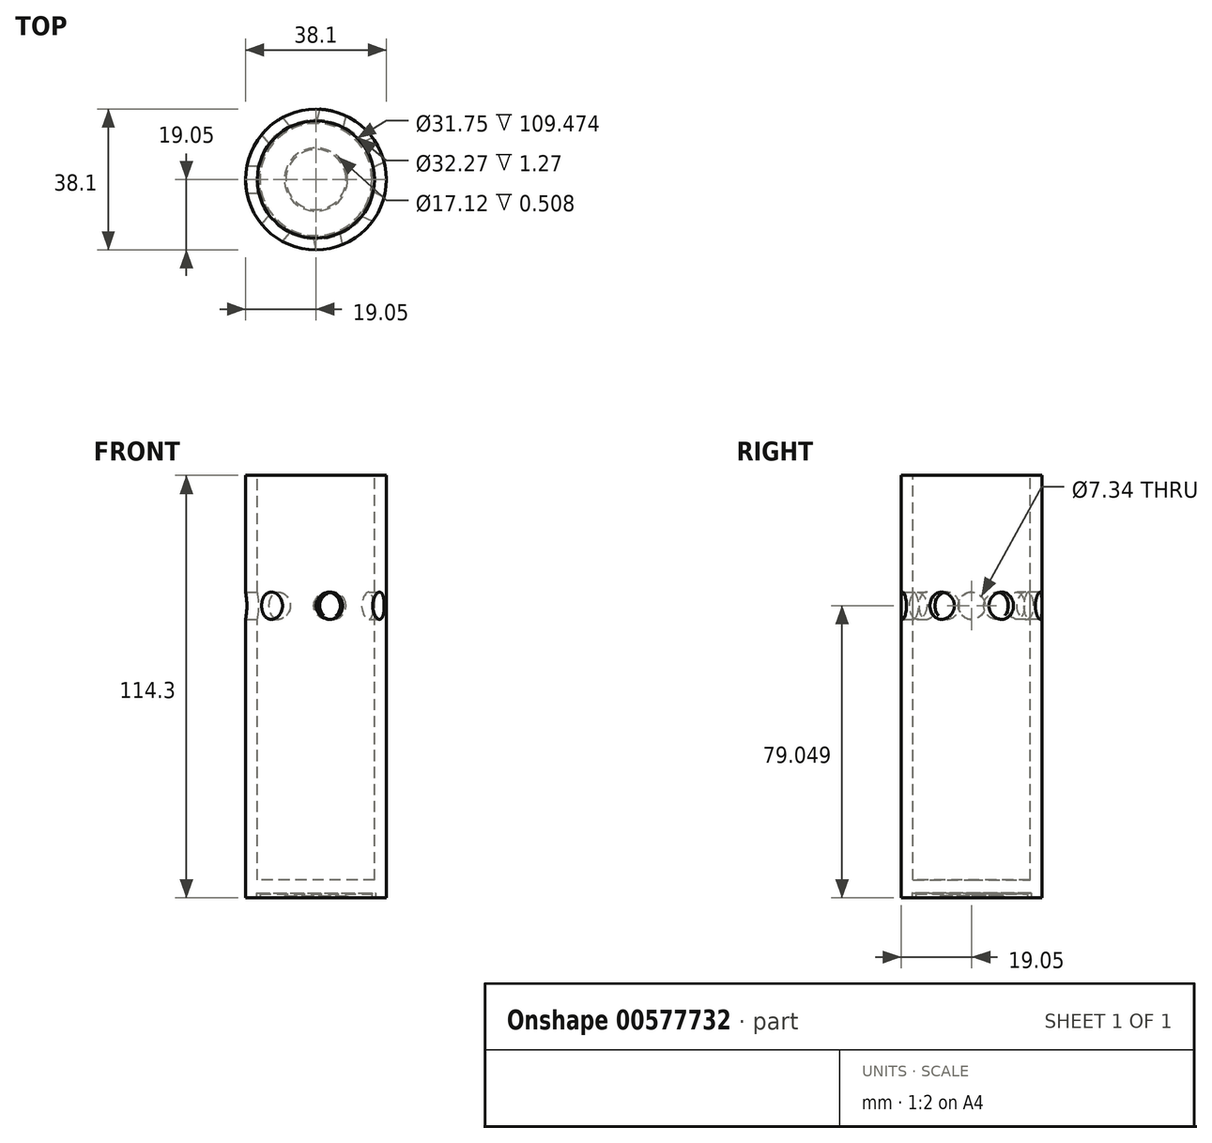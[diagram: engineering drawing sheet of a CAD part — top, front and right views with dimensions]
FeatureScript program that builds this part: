
annotation { "Feature Type Name" : "Feature", "Feature Type Description" : "" }
export const myFeature = defineFeature(function(context is Context, id is Id, definition is map)
    precondition{}
    {
        {
            var Q0;
            Q0=qCreatedBy(makeId("Top.planeOp"),FACE);
            var sketch = newSketch(context, id + "F0", { "sketchPlane" : qUnion([Q0])});
            skCircle(sketch, "E0", {"center": v(0, 0) * mm, "radius": 19.05 * mm});
            skSolve(sketch);
        }
        {
            var Q0;
            Q0=makeQuery(id+"F0.imprint","IMPRINT",FACE,{"disambiguationData":[TD([[makeQuery(id+"F0.imprint","IMPRINT",EDGE,{"derivedFrom":sQuery(id+"F0.wireOp",EDGE,"E0")}),1.0]])]});
            extrude(context, id + "F1", {"entities" : qUnion([Q0]), "depth" : 109.47 * mm, "offsetDistance" : 25.4 * mm});
        }
        {
            var Q0;
            Q0=makeQuery(id+"F1.opExtrude","CAP_FACE",FACE,{"disambiguationData":[OSD([sQuery(id+"F0.wireOp",EDGE,"E0")])],"isStart":false});
            var sketch = newSketch(context, id + "F2", { "sketchPlane" : qUnion([Q0])});
            skCircle(sketch, "E1", {"center": v(0, 0) * mm, "radius": 15.87 * mm});
            skSolve(sketch);
        }
        {
            var Q0;
            Q0=makeQuery(id+"F2.imprint","IMPRINT",FACE,{"disambiguationData":[TD([[makeQuery(id+"F2.imprint","IMPRINT",EDGE,{"derivedFrom":sQuery(id+"F2.wireOp",EDGE,"E1")}),1.0]])]});
            extrude(context, id + "F3", {"entities" : qUnion([Q0]), "operationType" : NewBodyOperationType.REMOVE, "oppositeDirection" : true, "depth" : 109.73 * mm, "offsetDistance" : 25.4 * mm});
        }
        {
            var Q0;
            Q0=qCreatedBy(makeId("Top.planeOp"),FACE);
            var sketch = newSketch(context, id + "F4", { "sketchPlane" : qUnion([Q0])});
            skCircle(sketch, "E2", {"center": v(0, 0) * mm, "radius": 19.05 * mm});
            skSolve(sketch);
        }
        {
            var Q0;
            Q0=makeQuery(id+"F4.imprint","IMPRINT",FACE,{"disambiguationData":[TD([[makeQuery(id+"F4.imprint","IMPRINT",EDGE,{"derivedFrom":sQuery(id+"F4.wireOp",EDGE,"E2")}),1.0]])]});
            extrude(context, id + "F5", {"entities" : qUnion([Q0]), "operationType" : NewBodyOperationType.ADD, "oppositeDirection" : true, "depth" : 1.27 * mm, "offsetDistance" : 25.4 * mm});
        }
        {
            var Q0;
            Q0=qCreatedBy(makeId("Right.planeOp"),FACE);
            var Q1;
            Q1=qCreatedBy(makeId("Front.planeOp"),FACE);
            cPlane(context, id + "F6", {"entities" : qUnion([Q0, Q1]), "cplaneType" : CPlaneType.MID_PLANE, "offset" : 25.4 * mm, "flipAlignment" : true, "width" : 152.4 * mm, "height" : 152.4 * mm});
        }
        {
            var Q0;
            Q0=qCreatedBy(makeId("Right.planeOp"),FACE);
            var Q1;
            Q1=qCreatedBy(makeId("Front.planeOp"),FACE);
            cPlane(context, id + "F7", {"entities" : qUnion([Q0, Q1]), "cplaneType" : CPlaneType.MID_PLANE, "offset" : 25.4 * mm, "width" : 152.4 * mm, "height" : 152.4 * mm});
        }
        {
            var Q0;
            Q0=qCreatedBy(id+"F7.planeOp",FACE);
            var Q1;
            Q1=qCreatedBy(makeId("Right.planeOp"),FACE);
            cPlane(context, id + "F8", {"entities" : qUnion([Q0, Q1]), "cplaneType" : CPlaneType.MID_PLANE, "offset" : 25.4 * mm, "flipAlignment" : true, "width" : 152.4 * mm, "height" : 152.4 * mm});
        }
        {
            var Q0;
            Q0=qCreatedBy(id+"F6.planeOp",FACE);
            var Q1;
            Q1=qCreatedBy(makeId("Right.planeOp"),FACE);
            cPlane(context, id + "F9", {"entities" : qUnion([Q0, Q1]), "cplaneType" : CPlaneType.MID_PLANE, "offset" : 25.4 * mm, "flipAlignment" : true, "width" : 152.4 * mm, "height" : 152.4 * mm});
        }
        {
            var Q0;
            Q0=qCreatedBy(makeId("Front.planeOp"),FACE);
            var Q1;
            Q1=qCreatedBy(id+"F7.planeOp",FACE);
            cPlane(context, id + "F10", {"entities" : qUnion([Q0, Q1]), "cplaneType" : CPlaneType.MID_PLANE, "offset" : 25.4 * mm, "width" : 152.4 * mm, "height" : 152.4 * mm});
        }
        {
            var Q0;
            Q0=qCreatedBy(makeId("Front.planeOp"),FACE);
            var Q1;
            Q1=qCreatedBy(id+"F6.planeOp",FACE);
            cPlane(context, id + "F11", {"entities" : qUnion([Q0, Q1]), "cplaneType" : CPlaneType.MID_PLANE, "offset" : 25.4 * mm, "flipAlignment" : true, "width" : 152.4 * mm, "height" : 152.4 * mm});
        }
        {
            var Q0;
            Q0=qCreatedBy(id+"F8.planeOp",FACE);
            var Q1;
            Q1=qCreatedBy(id+"F7.planeOp",FACE);
            cPlane(context, id + "F12", {"entities" : qUnion([Q0, Q1]), "cplaneType" : CPlaneType.MID_PLANE, "offset" : 25.4 * mm, "flipAlignment" : true, "width" : 152.4 * mm, "height" : 152.4 * mm});
        }
        {
            var Q0;
            Q0=qCreatedBy(id+"F9.planeOp",FACE);
            var Q1;
            Q1=qCreatedBy(id+"F6.planeOp",FACE);
            cPlane(context, id + "F13", {"entities" : qUnion([Q0, Q1]), "cplaneType" : CPlaneType.MID_PLANE, "offset" : 25.4 * mm, "flipAlignment" : true, "width" : 152.4 * mm, "height" : 152.4 * mm});
        }
        {
            var Q0;
            Q0=qCreatedBy(id+"F13.planeOp",FACE);
            var Q1;
            Q1=qCreatedBy(id+"F9.planeOp",FACE);
            cPlane(context, id + "F14", {"entities" : qUnion([Q0, Q1]), "cplaneType" : CPlaneType.MID_PLANE, "offset" : 25.4 * mm, "flipAlignment" : true, "width" : 152.4 * mm, "height" : 152.4 * mm});
        }
        {
            var Q0;
            Q0=qCreatedBy(id+"F8.planeOp",FACE);
            var Q1;
            Q1=qCreatedBy(id+"F12.planeOp",FACE);
            cPlane(context, id + "F15", {"entities" : qUnion([Q0, Q1]), "cplaneType" : CPlaneType.MID_PLANE, "offset" : 25.4 * mm, "flipAlignment" : true, "width" : 152.4 * mm, "height" : 152.4 * mm});
        }
        {
            var Q0;
            Q0=qCreatedBy(id+"F15.planeOp",FACE);
            var Q1;
            Q1=qCreatedBy(id+"F8.planeOp",FACE);
            cPlane(context, id + "F16", {"entities" : qUnion([Q0, Q1]), "cplaneType" : CPlaneType.MID_PLANE, "offset" : 25.4 * mm, "flipAlignment" : true, "width" : 152.4 * mm, "height" : 152.4 * mm});
        }
        {
            var Q0;
            Q0=qCreatedBy(id+"F9.planeOp",FACE);
            var Q1;
            Q1=qCreatedBy(id+"F14.planeOp",FACE);
            cPlane(context, id + "F17", {"entities" : qUnion([Q0, Q1]), "cplaneType" : CPlaneType.MID_PLANE, "offset" : 25.4 * mm, "flipAlignment" : true, "width" : 152.4 * mm, "height" : 152.4 * mm});
        }
        {
            var Q0;
            Q0=qCreatedBy(makeId("Front.planeOp"),FACE);
            var Q1;
            Q1=qCreatedBy(id+"F11.planeOp",FACE);
            cPlane(context, id + "F18", {"entities" : qUnion([Q0, Q1]), "cplaneType" : CPlaneType.MID_PLANE, "offset" : 25.4 * mm, "flipAlignment" : true, "width" : 152.4 * mm, "height" : 152.4 * mm});
        }
        {
            var Q0;
            Q0=qCreatedBy(id+"F10.planeOp",FACE);
            var Q1;
            Q1=qCreatedBy(id+"F7.planeOp",FACE);
            cPlane(context, id + "F19", {"entities" : qUnion([Q0, Q1]), "cplaneType" : CPlaneType.MID_PLANE, "offset" : 25.4 * mm, "width" : 152.4 * mm, "height" : 152.4 * mm});
        }
        {
            var Q0;
            Q0=qCreatedBy(id+"F19.planeOp",FACE);
            var Q1;
            Q1=qCreatedBy(id+"F7.planeOp",FACE);
            cPlane(context, id + "F20", {"entities" : qUnion([Q0, Q1]), "cplaneType" : CPlaneType.MID_PLANE, "offset" : 25.4 * mm, "width" : 152.4 * mm, "height" : 152.4 * mm});
        }
        {
            var Q0;
            Q0=qCreatedBy(id+"F6.planeOp",FACE);
            var Q1;
            Q1=qCreatedBy(id+"F11.planeOp",FACE);
            cPlane(context, id + "F21", {"entities" : qUnion([Q0, Q1]), "cplaneType" : CPlaneType.MID_PLANE, "offset" : 25.4 * mm, "flipAlignment" : true, "width" : 152.4 * mm, "height" : 152.4 * mm});
        }
        {
            var Q0;
            Q0=qCreatedBy(id+"F6.planeOp",FACE);
            var Q1;
            Q1=qCreatedBy(id+"F21.planeOp",FACE);
            cPlane(context, id + "F22", {"entities" : qUnion([Q0, Q1]), "cplaneType" : CPlaneType.MID_PLANE, "offset" : 25.4 * mm, "flipAlignment" : true, "width" : 152.4 * mm, "height" : 152.4 * mm});
        }
        {
            var Q0;
            Q0=qCreatedBy(id+"F20.planeOp",FACE);
            var Q1;
            Q1=qCreatedBy(id+"F18.planeOp",FACE);
            cPlane(context, id + "F23", {"entities" : qUnion([Q0, Q1]), "cplaneType" : CPlaneType.MID_PLANE, "offset" : 25.4 * mm, "flipAlignment" : true, "width" : 152.4 * mm, "height" : 152.4 * mm});
        }
        {
            var Q0;
            Q0=qCreatedBy(id+"F17.planeOp",FACE);
            var sketch = newSketch(context, id + "F24", { "sketchPlane" : qUnion([Q0])});
            skCircle(sketch, "E3", {"center": v(0, 74.22) * mm, "radius": 3.67 * mm});
            skLineSegment(sketch, "E4", {"start": v(0, 74.22) * mm, "end": v(0, 0) * mm});
            skSolve(sketch);
        }
        {
            var Q0;
            Q0 = qSketchRegion(id + "F24", true);
            extrude(context, id + "F25", {"entities" : qUnion([Q0]), "operationType" : NewBodyOperationType.ADD, "depth" : 25.4 * mm, "offsetDistance" : 25.4 * mm});
        }
        {
            var Q0;
            Q0=makeQuery(id+"F25.opExtrude","CAP_FACE",FACE,{"disambiguationData":[OSD([sQuery(id+"F24.wireOp",EDGE,"E3")])],"isStart":false});
            extrude(context, id + "F26", {"entities" : qUnion([Q0]), "operationType" : NewBodyOperationType.REMOVE, "oppositeDirection" : true, "depth" : 32 * mm, "offsetDistance" : 25.4 * mm});
        }
        {
            var Q0;
            Q0=qCreatedBy(id+"F16.planeOp",FACE);
            var sketch = newSketch(context, id + "F27", { "sketchPlane" : qUnion([Q0])});
            skCircle(sketch, "E5", {"center": v(0, 74.22) * mm, "radius": 3.67 * mm});
            skLineSegment(sketch, "E6", {"start": v(0, 74.22) * mm, "end": v(0, 0) * mm});
            skSolve(sketch);
        }
        {
            var Q0;
            Q0 = qSketchRegion(id + "F27", true);
            extrude(context, id + "F28", {"entities" : qUnion([Q0]), "operationType" : NewBodyOperationType.REMOVE, "depth" : 45.47 * mm, "offsetDistance" : 25.4 * mm});
        }
        {
            var Q0;
            Q0=qCreatedBy(id+"F23.planeOp",FACE);
            var sketch = newSketch(context, id + "F29", { "sketchPlane" : qUnion([Q0])});
            skCircle(sketch, "E7", {"center": v(0, 74.22) * mm, "radius": 3.67 * mm});
            skLineSegment(sketch, "E8", {"start": v(0, 74.22) * mm, "end": v(0, 0) * mm});
            skSolve(sketch);
        }
        {
            var Q0;
            Q0 = qSketchRegion(id + "F29", true);
            extrude(context, id + "F30", {"entities" : qUnion([Q0]), "operationType" : NewBodyOperationType.REMOVE, "oppositeDirection" : true, "depth" : 34.04 * mm, "offsetDistance" : 25.4 * mm});
        }
        {
            var Q0;
            Q0=qCreatedBy(id+"F22.planeOp",FACE);
            var sketch = newSketch(context, id + "F31", { "sketchPlane" : qUnion([Q0])});
            skCircle(sketch, "E9", {"center": v(0, 74.22) * mm, "radius": 3.67 * mm});
            skLineSegment(sketch, "E10", {"start": v(0, 74.22) * mm, "end": v(0, 0) * mm});
            skSolve(sketch);
        }
        {
            var Q0;
            Q0 = qSketchRegion(id + "F31", true);
            extrude(context, id + "F32", {"entities" : qUnion([Q0]), "operationType" : NewBodyOperationType.REMOVE, "oppositeDirection" : true, "depth" : 25.4 * mm, "offsetDistance" : 25.4 * mm});
        }
        {
            var Q0;
            Q0=qCreatedBy(makeId("Right.planeOp"),FACE);
            var sketch = newSketch(context, id + "F33", { "sketchPlane" : qUnion([Q0])});
            skCircle(sketch, "E11", {"center": v(0, 74.22) * mm, "radius": 3.67 * mm});
            skLineSegment(sketch, "E12", {"start": v(0, 74.22) * mm, "end": v(0, 0) * mm});
            skSolve(sketch);
        }
        {
            var Q0;
            Q0 = qSketchRegion(id + "F33", true);
            extrude(context, id + "F34", {"entities" : qUnion([Q0]), "operationType" : NewBodyOperationType.REMOVE, "oppositeDirection" : true, "depth" : 25.4 * mm, "offsetDistance" : 25.4 * mm});
        }
        {
            var Q0;
            Q0=qCreatedBy(id+"F20.planeOp",FACE);
            var sketch = newSketch(context, id + "F35", { "sketchPlane" : qUnion([Q0])});
            skCircle(sketch, "E13", {"center": v(0, 74.22) * mm, "radius": 3.67 * mm});
            skLineSegment(sketch, "E14", {"start": v(0, 74.22) * mm, "end": v(0, 0) * mm});
            skSolve(sketch);
        }
        {
            var Q0;
            Q0 = qSketchRegion(id + "F35", true);
            extrude(context, id + "F36", {"entities" : qUnion([Q0]), "operationType" : NewBodyOperationType.REMOVE, "depth" : 53.1 * mm, "offsetDistance" : 25.4 * mm});
        }
        {
            var Q0;
            Q0=qCreatedBy(id+"F18.planeOp",FACE);
            var sketch = newSketch(context, id + "F37", { "sketchPlane" : qUnion([Q0])});
            skCircle(sketch, "E15", {"center": v(0, 74.22) * mm, "radius": 3.67 * mm});
            skLineSegment(sketch, "E16", {"start": v(0, 74.22) * mm, "end": v(0, 0) * mm});
            skSolve(sketch);
        }
        {
            var Q0;
            Q0 = qSketchRegion(id + "F37", true);
            extrude(context, id + "F38", {"entities" : qUnion([Q0]), "operationType" : NewBodyOperationType.REMOVE, "depth" : 65.8 * mm, "offsetDistance" : 25.4 * mm});
        }
        {
            var Q0;
            Q0=qCreatedBy(makeId("Top.planeOp"),FACE);
            var sketch = newSketch(context, id + "F39", { "sketchPlane" : qUnion([Q0])});
            skCircle(sketch, "E17", {"center": v(0, 0) * mm, "radius": 19.05 * mm});
            skSolve(sketch);
        }
        {
            var Q0;
            Q0 = qSketchRegion(id + "F39", true);
            extrude(context, id + "F40", {"entities" : qUnion([Q0]), "operationType" : NewBodyOperationType.ADD, "oppositeDirection" : true, "depth" : 4.83 * mm, "offsetDistance" : 25.4 * mm});
        }
        {
            var Q0;
            Q0=makeQuery(id+"F40.opExtrude","CAP_FACE",FACE,{"disambiguationData":[OSD([sQuery(id+"F39.wireOp",EDGE,"E17")])],"isStart":false});
            var sketch = newSketch(context, id + "F41", { "sketchPlane" : qUnion([Q0])});
            skCircle(sketch, "E18", {"center": v(0, 0) * mm, "radius": 16.14 * mm});
            skCircle(sketch, "E19", {"center": v(0, 0) * mm, "radius": 15.14 * mm});
            skSolve(sketch);
        }
        {
            var Q0;
            Q0=makeQuery(id+"F41.imprint","IMPRINT",FACE,{"disambiguationData":[TD([[makeQuery(id+"F41.imprint","IMPRINT",EDGE,{"derivedFrom":sQuery(id+"F41.wireOp",EDGE,"E18")}),1.0]])]});
            extrude(context, id + "F42", {"entities" : qUnion([Q0]), "operationType" : NewBodyOperationType.REMOVE, "oppositeDirection" : true, "depth" : 1.27 * mm, "offsetDistance" : 25.4 * mm});
        }
        {
            var Q0;
            Q0=makeQuery(id+"F42.boolean.opBoolean","COPY",EDGE,{"derivedFrom":makeQuery(id+"F42.opExtrude","CAP_EDGE",EDGE,{"disambiguationData":[OSD([sQuery(id+"F41.wireOp",EDGE,"E19")])],"isStart":false})});
            chamfer(context, id + "F43", {"entities" : qUnion([Q0]), "width" : 0.25 * mm, "tangentPropagation" : true});
        }
        {
            var Q0;
            Q0=makeQuery(id+"F42.boolean.opBoolean","SPLIT",FACE,{"disambiguationData":[TD([makeQuery(id+"F42.opExtrude","SWEPT_FACE",FACE,{"disambiguationData":[OSD([sQuery(id+"F41.wireOp",EDGE,"E19")])]})])],"derivedFrom":makeQuery(id+"F40.opExtrude","CAP_FACE",FACE,{"disambiguationData":[OSD([sQuery(id+"F39.wireOp",EDGE,"E17")])],"isStart":false})});
            var sketch = newSketch(context, id + "F44", { "sketchPlane" : qUnion([Q0])});
            skCircle(sketch, "E20", {"center": v(0, 0) * mm, "radius": 8.12 * mm});
            skCircle(sketch, "E21", {"center": v(0, 0) * mm, "radius": 8.56 * mm});
            skSolve(sketch);
        }
        {
            var Q0;
            Q0=makeQuery(id+"F44.imprint","IMPRINT",FACE,{"disambiguationData":[TD([[makeQuery(id+"F44.imprint","IMPRINT",EDGE,{"derivedFrom":sQuery(id+"F44.wireOp",EDGE,"E20")}),-1.0]])]});
            extrude(context, id + "F45", {"entities" : qUnion([Q0]), "operationType" : NewBodyOperationType.REMOVE, "oppositeDirection" : true, "depth" : 0.5 * mm, "offsetDistance" : 25.4 * mm});
        }
    });
